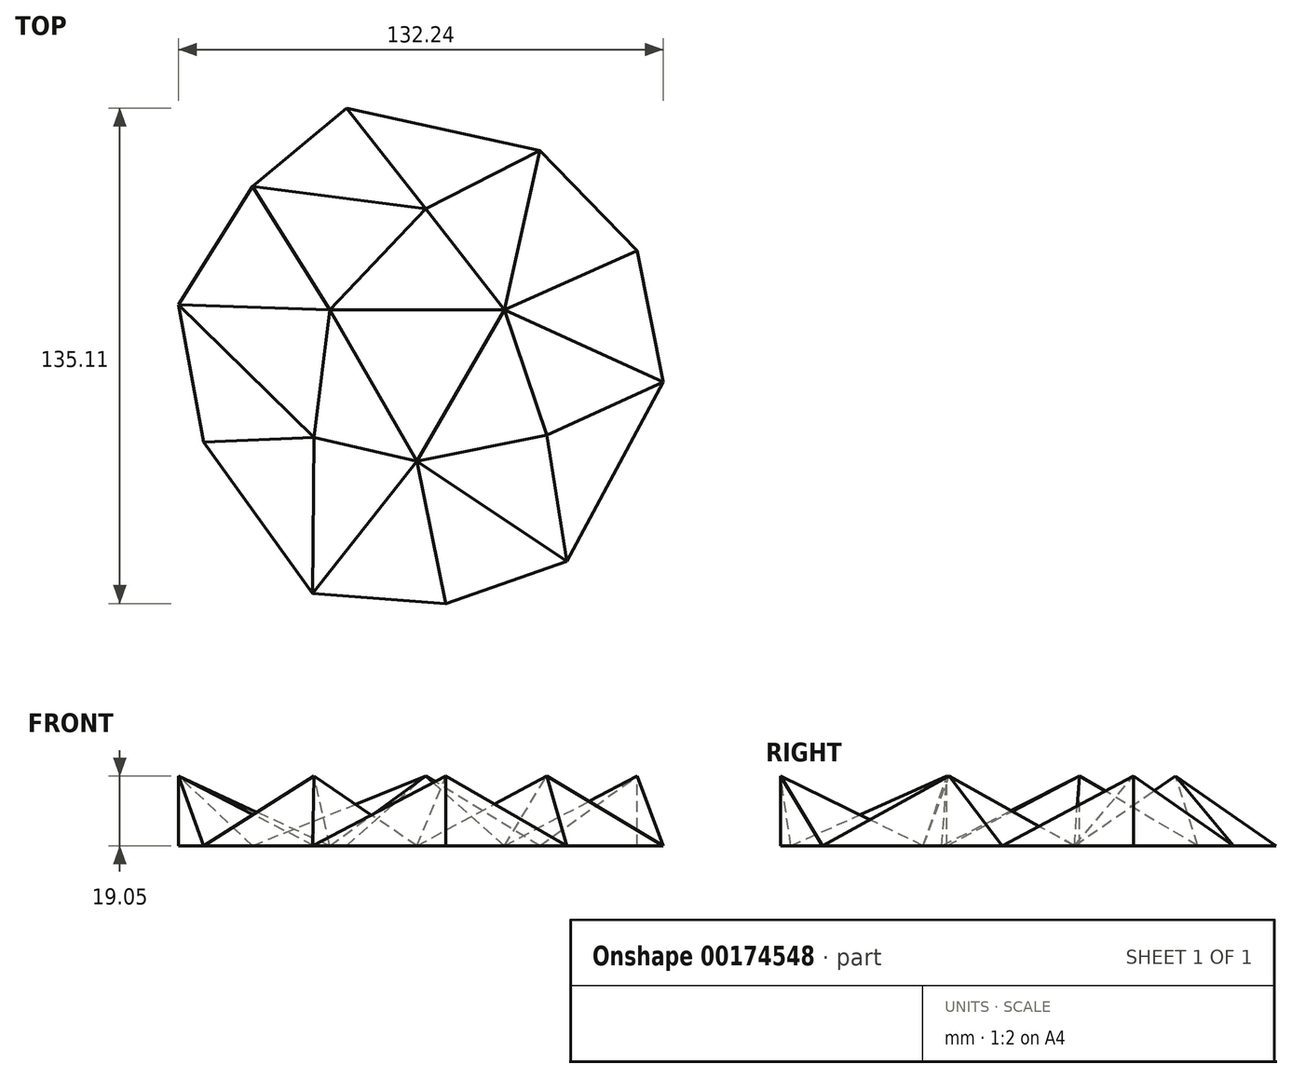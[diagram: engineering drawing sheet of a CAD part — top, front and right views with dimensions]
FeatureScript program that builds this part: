
annotation { "Feature Type Name" : "Feature", "Feature Type Description" : "" }
export const myFeature = defineFeature(function(context is Context, id is Id, definition is map)
    precondition{}
    {
        {
            var Q0;
            Q0=qCreatedBy(makeId("Top.planeOp"),FACE);
            var sketch = newSketch(context, id + "F0", { "sketchPlane" : qUnion([Q0])});
            skCircle(sketch, "E0.cCircle", {"center": v(0, 0) * mm, "radius": 13.75 * mm, "construction": true});
            skLineSegment(sketch, "E0.0", {"start": v(0, -27.5) * mm, "end": v(-23.81, 13.75) * mm});
            skLineSegment(sketch, "E0.1", {"start": v(-23.81, 13.75) * mm, "end": v(23.81, 13.75) * mm});
            skLineSegment(sketch, "E0.2", {"start": v(23.81, 13.75) * mm, "end": v(0, -27.5) * mm});
            skLineSegment(sketch, "E1", {"start": v(0, 0) * mm, "end": v(0, -27.5) * mm, "construction": true});
            skLineSegment(sketch, "E2", {"start": v(-19.24, 68.72) * mm, "end": v(33.48, 57.13) * mm});
            skLineSegment(sketch, "E3", {"start": v(33.48, 57.13) * mm, "end": v(60.1, 29.87) * mm});
            skLineSegment(sketch, "E4", {"start": v(60.1, 29.87) * mm, "end": v(67.17, -5.96) * mm});
            skLineSegment(sketch, "E5", {"start": v(67.17, -5.96) * mm, "end": v(40.86, -54.92) * mm});
            skLineSegment(sketch, "E6", {"start": v(40.86, -54.92) * mm, "end": v(7.88, -66.4) * mm});
            skLineSegment(sketch, "E7", {"start": v(7.88, -66.4) * mm, "end": v(-28.54, -63.62) * mm});
            skLineSegment(sketch, "E8", {"start": v(-28.54, -63.62) * mm, "end": v(-58.24, -22.4) * mm});
            skLineSegment(sketch, "E9", {"start": v(-58.24, -22.4) * mm, "end": v(-65.07, 15.08) * mm});
            skLineSegment(sketch, "E10", {"start": v(-65.07, 15.08) * mm, "end": v(-44.87, 47.39) * mm});
            skLineSegment(sketch, "E11", {"start": v(-44.87, 47.39) * mm, "end": v(-19.24, 68.72) * mm});
            skLineSegment(sketch, "E12", {"start": v(33.48, 57.13) * mm, "end": v(23.81, 13.75) * mm});
            skLineSegment(sketch, "E13", {"start": v(60.1, 29.87) * mm, "end": v(23.81, 13.75) * mm});
            skLineSegment(sketch, "E14", {"start": v(23.81, 13.75) * mm, "end": v(67.17, -5.96) * mm});
            skLineSegment(sketch, "E15", {"start": v(-44.87, 47.39) * mm, "end": v(-23.81, 13.75) * mm});
            skLineSegment(sketch, "E16", {"start": v(-65.07, 15.08) * mm, "end": v(-23.81, 13.75) * mm});
            skLineSegment(sketch, "E17", {"start": v(-28.54, -63.62) * mm, "end": v(0, -27.5) * mm});
            skLineSegment(sketch, "E18", {"start": v(7.88, -66.4) * mm, "end": v(0, -27.5) * mm});
            skLineSegment(sketch, "E19", {"start": v(40.86, -54.92) * mm, "end": v(0, -27.5) * mm});
            skLineSegment(sketch, "E20", {"start": v(-23.81, 13.75) * mm, "end": v(-28.1, -21.08) * mm});
            skLineSegment(sketch, "E21", {"start": v(-28.1, -21.08) * mm, "end": v(-65.07, 15.08) * mm});
            skLineSegment(sketch, "E22", {"start": v(-58.24, -22.4) * mm, "end": v(-28.1, -21.08) * mm});
            skLineSegment(sketch, "E23", {"start": v(-28.54, -63.62) * mm, "end": v(-28.1, -21.08) * mm});
            skLineSegment(sketch, "E24", {"start": v(-28.1, -21.08) * mm, "end": v(0, -27.5) * mm});
            skLineSegment(sketch, "E25", {"start": v(23.81, 13.75) * mm, "end": v(35.38, -20.43) * mm});
            skLineSegment(sketch, "E26", {"start": v(35.38, -20.43) * mm, "end": v(67.17, -5.96) * mm});
            skLineSegment(sketch, "E27", {"start": v(40.86, -54.92) * mm, "end": v(35.38, -20.43) * mm});
            skLineSegment(sketch, "E28", {"start": v(35.38, -20.43) * mm, "end": v(0, -27.5) * mm});
            skLineSegment(sketch, "E29", {"start": v(-19.24, 68.72) * mm, "end": v(2.36, 41.28) * mm});
            skLineSegment(sketch, "E30", {"start": v(2.36, 41.28) * mm, "end": v(-23.81, 13.75) * mm});
            skLineSegment(sketch, "E31", {"start": v(33.48, 57.13) * mm, "end": v(2.36, 41.28) * mm});
            skLineSegment(sketch, "E32", {"start": v(23.81, 13.75) * mm, "end": v(2.36, 41.28) * mm});
            skLineSegment(sketch, "E33", {"start": v(-44.87, 47.39) * mm, "end": v(2.36, 41.28) * mm});
            skSolve(sketch);
        }
        {
            var Q0;
            Q0=qCreatedBy(makeId("Top.planeOp"),FACE);
            cPlane(context, id + "F1", {"entities" : qUnion([Q0]), "cplaneType" : CPlaneType.OFFSET, "offset" : 19.05 * mm, "width" : 152.4 * mm, "height" : 152.4 * mm});
        }
        {
            var Q0;
            Q0=qCreatedBy(id+"F1.planeOp",FACE);
            var sketch = newSketch(context, id + "F2", { "sketchPlane" : qUnion([Q0])});
            skPoint(sketch, "E34.0", {"position": v(-23.81, 13.75) * mm});
            skPoint(sketch, "E35.0", {"position": v(2.36, 41.28) * mm});
            skPoint(sketch, "E36.0", {"position": v(23.81, 13.75) * mm});
            skPoint(sketch, "E37.0", {"position": v(0, -27.5) * mm});
            skPoint(sketch, "E38.0", {"position": v(-28.1, -21.08) * mm});
            skPoint(sketch, "E39.0", {"position": v(35.38, -20.43) * mm});
            skPoint(sketch, "E40.0", {"position": v(67.17, -5.96) * mm});
            skPoint(sketch, "E41.0", {"position": v(60.1, 29.87) * mm});
            skPoint(sketch, "E42.0", {"position": v(33.48, 57.13) * mm});
            skPoint(sketch, "E43.0", {"position": v(-44.87, 47.39) * mm});
            skPoint(sketch, "E44.0", {"position": v(-65.07, 15.08) * mm});
            skPoint(sketch, "E45.0", {"position": v(-58.24, -22.4) * mm});
            skPoint(sketch, "E46.0", {"position": v(-28.54, -63.62) * mm});
            skPoint(sketch, "E47.0", {"position": v(7.88, -66.4) * mm});
            skPoint(sketch, "E48.0", {"position": v(40.86, -54.92) * mm});
            skPoint(sketch, "E49.0", {"position": v(-19.24, 68.72) * mm});
            skSolve(sketch);
        }
        {
            var Q0;
            Q0=qCreatedBy(makeId("Top.planeOp"),FACE);
            var sketch = newSketch(context, id + "F3", { "sketchPlane" : qUnion([Q0])});
            skLineSegment(sketch, "E50.0", {"start": v(-19.24, 68.72) * mm, "end": v(33.48, 57.13) * mm});
            skLineSegment(sketch, "E51.0", {"start": v(-44.87, 47.39) * mm, "end": v(-19.24, 68.72) * mm});
            skLineSegment(sketch, "E52.0", {"start": v(-44.87, 47.39) * mm, "end": v(-23.81, 13.75) * mm});
            skLineSegment(sketch, "E53.0", {"start": v(-23.81, 13.75) * mm, "end": v(23.81, 13.75) * mm});
            skLineSegment(sketch, "E54.0", {"start": v(33.48, 57.13) * mm, "end": v(23.81, 13.75) * mm});
            skSolve(sketch);
        }
        {
            var Q0;
            Q0 = qConstructionFilter(qBodyType(qCreatedBy(id + "F3" ,EDGE), BodyType.WIRE), ConstructionObject.NO);
            var Q1;
            Q1=sQuery(id+"F2.wireOp",VERTEX,"E35.0");
            loft(context, id + "F4", {"bodyType" : ToolBodyType.SURFACE, "wireProfilesArray" : [{ "wireProfileEntities" : qUnion([Q0]) }, { "wireProfileEntities" : qUnion([Q1]) }]});
        }
        {
            var Q0;
            Q0=qCreatedBy(makeId("Top.planeOp"),FACE);
            var sketch = newSketch(context, id + "F5", { "sketchPlane" : qUnion([Q0])});
            skLineSegment(sketch, "E55.0", {"start": v(33.48, 57.13) * mm, "end": v(23.81, 13.75) * mm});
            skLineSegment(sketch, "E56.0", {"start": v(23.81, 13.75) * mm, "end": v(67.17, -5.96) * mm});
            skLineSegment(sketch, "E57.0", {"start": v(60.1, 29.87) * mm, "end": v(67.17, -5.96) * mm});
            skLineSegment(sketch, "E58.0", {"start": v(33.48, 57.13) * mm, "end": v(60.1, 29.87) * mm});
            skSolve(sketch);
        }
        {
            var Q0;
            Q0 = qSketchRegion(id + "F5", true);
            var Q1;
            Q1 = qConstructionFilter(qBodyType(qCreatedBy(id + "F5" ,EDGE), BodyType.WIRE), ConstructionObject.NO);
            var Q2;
            Q2=sQuery(id+"F2.wireOp",VERTEX,"E41.0");
            loft(context, id + "F6", {"bodyType" : ToolBodyType.SURFACE, "sheetProfilesArray" : [{ "sheetProfileEntities" : qUnion([Q0]) }], "wireProfilesArray" : [{ "wireProfileEntities" : qUnion([Q1]) }, { "wireProfileEntities" : qUnion([Q2]) }]});
        }
        {
            var Q0;
            Q0=qCreatedBy(makeId("Top.planeOp"),FACE);
            var sketch = newSketch(context, id + "F7", { "sketchPlane" : qUnion([Q0])});
            skLineSegment(sketch, "E59.0", {"start": v(23.81, 13.75) * mm, "end": v(0, -27.5) * mm});
            skLineSegment(sketch, "E60.0", {"start": v(23.81, 13.75) * mm, "end": v(67.17, -5.96) * mm});
            skLineSegment(sketch, "E61.0", {"start": v(67.17, -5.96) * mm, "end": v(40.86, -54.92) * mm});
            skLineSegment(sketch, "E62.0", {"start": v(40.86, -54.92) * mm, "end": v(0, -27.5) * mm});
            skSolve(sketch);
        }
        {
            var Q0;
            Q0 = qConstructionFilter(qBodyType(qCreatedBy(id + "F7" ,EDGE), BodyType.WIRE), ConstructionObject.NO);
            var Q1;
            Q1=sQuery(id+"F2.wireOp",VERTEX,"E39.0");
            loft(context, id + "F8", {"bodyType" : ToolBodyType.SURFACE, "wireProfilesArray" : [{ "wireProfileEntities" : qUnion([Q0]) }, { "wireProfileEntities" : qUnion([Q1]) }]});
        }
        {
            var Q0;
            Q0=qCreatedBy(makeId("Top.planeOp"),FACE);
            var sketch = newSketch(context, id + "F9", { "sketchPlane" : qUnion([Q0])});
            skLineSegment(sketch, "E63.0", {"start": v(40.86, -54.92) * mm, "end": v(0, -27.5) * mm});
            skLineSegment(sketch, "E64.0", {"start": v(-28.54, -63.62) * mm, "end": v(0, -27.5) * mm});
            skLineSegment(sketch, "E65.0", {"start": v(7.88, -66.4) * mm, "end": v(-28.54, -63.62) * mm});
            skLineSegment(sketch, "E66.0", {"start": v(40.86, -54.92) * mm, "end": v(7.88, -66.4) * mm});
            skSolve(sketch);
        }
        {
            var Q0;
            Q0 = qConstructionFilter(qBodyType(qCreatedBy(id + "F9" ,EDGE), BodyType.WIRE), ConstructionObject.NO);
            var Q1;
            Q1=sQuery(id+"F2.wireOp",VERTEX,"E47.0");
            loft(context, id + "F10", {"bodyType" : ToolBodyType.SURFACE, "wireProfilesArray" : [{ "wireProfileEntities" : qUnion([Q0]) }, { "wireProfileEntities" : qUnion([Q1]) }]});
        }
        {
            var Q0;
            Q0=qCreatedBy(makeId("Top.planeOp"),FACE);
            var sketch = newSketch(context, id + "F11", { "sketchPlane" : qUnion([Q0])});
            skLineSegment(sketch, "E67.0", {"start": v(-23.81, 13.75) * mm, "end": v(-28.1, -21.08) * mm});
            skLineSegment(sketch, "E68.0", {"start": v(-58.24, -22.4) * mm, "end": v(-28.1, -21.08) * mm});
            skLineSegment(sketch, "E69.0", {"start": v(-28.54, -63.62) * mm, "end": v(-58.24, -22.4) * mm});
            skLineSegment(sketch, "E70.0", {"start": v(-28.54, -63.62) * mm, "end": v(0, -27.5) * mm});
            skLineSegment(sketch, "E71.0", {"start": v(0, -27.5) * mm, "end": v(-23.81, 13.75) * mm});
            skSolve(sketch);
        }
        {
            var Q0;
            Q0 = qConstructionFilter(qBodyType(qCreatedBy(id + "F11" ,EDGE), BodyType.WIRE), ConstructionObject.NO);
            var Q1;
            Q1=sQuery(id+"F2.wireOp",VERTEX,"E38.0");
            loft(context, id + "F12", {"bodyType" : ToolBodyType.SURFACE, "wireProfilesArray" : [{ "wireProfileEntities" : qUnion([Q0]) }, { "wireProfileEntities" : qUnion([Q1]) }]});
        }
        {
            var Q0;
            Q0=qCreatedBy(makeId("Top.planeOp"),FACE);
            var sketch = newSketch(context, id + "F13", { "sketchPlane" : qUnion([Q0])});
            skLineSegment(sketch, "E72.0", {"start": v(-44.87, 47.39) * mm, "end": v(-23.81, 13.75) * mm});
            skLineSegment(sketch, "E73.0", {"start": v(-65.07, 15.08) * mm, "end": v(-44.87, 47.39) * mm});
            skLineSegment(sketch, "E74.0", {"start": v(-58.24, -22.4) * mm, "end": v(-65.07, 15.08) * mm});
            skLineSegment(sketch, "E75.0", {"start": v(-58.24, -22.4) * mm, "end": v(-28.1, -21.08) * mm});
            skLineSegment(sketch, "E76.0", {"start": v(-23.81, 13.75) * mm, "end": v(-28.1, -21.08) * mm});
            skSolve(sketch);
        }
        {
            var Q0;
            Q0 = qConstructionFilter(qBodyType(qCreatedBy(id + "F13" ,EDGE), BodyType.WIRE), ConstructionObject.NO);
            var Q1;
            Q1=sQuery(id+"F2.wireOp",VERTEX,"E44.0");
            loft(context, id + "F14", {"bodyType" : ToolBodyType.SURFACE, "wireProfilesArray" : [{ "wireProfileEntities" : qUnion([Q0]) }, { "wireProfileEntities" : qUnion([Q1]) }]});
        }
    });
